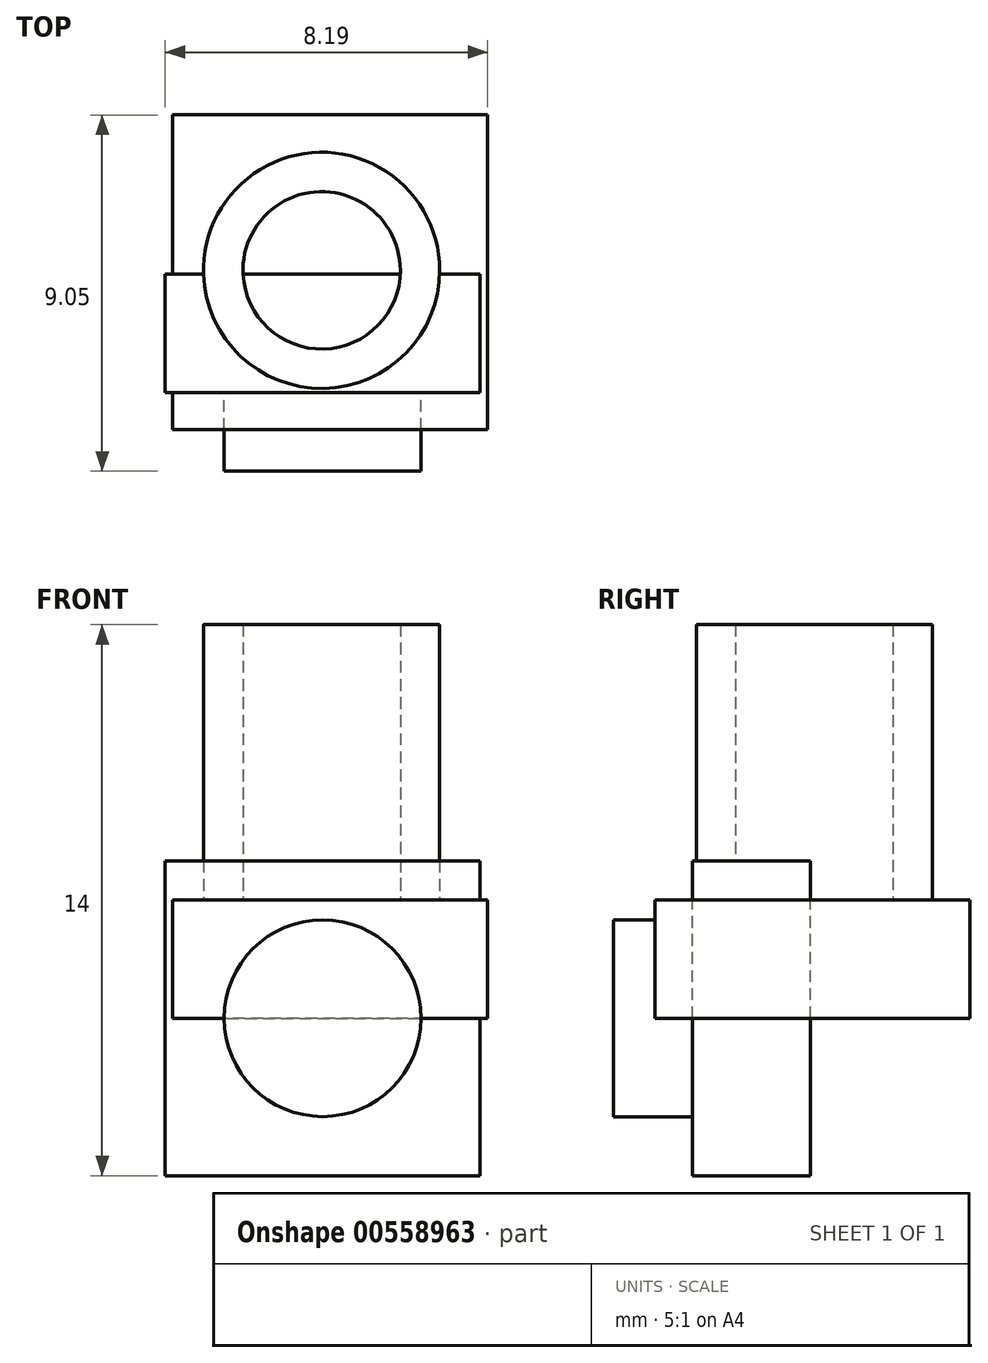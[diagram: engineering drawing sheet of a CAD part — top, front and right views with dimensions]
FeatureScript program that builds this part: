
annotation { "Feature Type Name" : "Feature", "Feature Type Description" : "" }
export const myFeature = defineFeature(function(context is Context, id is Id, definition is map)
    precondition{}
    {
        {
            var Q0;
            Q0=qCreatedBy(makeId("Front.planeOp"),FACE);
            var sketch = newSketch(context, id + "F0", { "sketchPlane" : qUnion([Q0])});
            skLineSegment(sketch, "E0.bottom", {"start": v(4, 4) * mm, "end": v(-4, 4) * mm});
            skLineSegment(sketch, "E0.top", {"start": v(4, -4) * mm, "end": v(-4, -4) * mm});
            skLineSegment(sketch, "E0.left", {"start": v(4, 4) * mm, "end": v(4, -4) * mm});
            skLineSegment(sketch, "E0.right", {"start": v(-4, 4) * mm, "end": v(-4, -4) * mm});
            skPoint(sketch, "E0.middle", {"position": v(0, 0) * mm});
            skSolve(sketch);
        }
        {
            var Q0;
            Q0 = qSketchRegion(id + "F0", true);
            extrude(context, id + "F1", {"entities" : qUnion([Q0]), "depth" : 3 * mm, "offsetDistance" : 25 * mm});
        }
        {
            var Q0;
            Q0=qCreatedBy(makeId("Front.planeOp"),FACE);
            var sketch = newSketch(context, id + "F2", { "sketchPlane" : qUnion([Q0])});
            skCircle(sketch, "E1", {"center": v(0, 0) * mm, "radius": 2.5 * mm});
            skSolve(sketch);
        }
        {
            var Q0;
            Q0 = qSketchRegion(id + "F2", true);
            extrude(context, id + "F3", {"entities" : qUnion([Q0]), "operationType" : NewBodyOperationType.ADD, "depth" : 5 * mm, "offsetDistance" : 25 * mm});
        }
        {
            var Q0;
            Q0=qCreatedBy(makeId("Top.planeOp"),FACE);
            var sketch = newSketch(context, id + "F4", { "sketchPlane" : qUnion([Q0])});
            skLineSegment(sketch, "E2.bottom", {"start": v(-3.81, 4.05) * mm, "end": v(4.19, 4.05) * mm});
            skLineSegment(sketch, "E2.top", {"start": v(-3.81, -3.95) * mm, "end": v(4.19, -3.95) * mm});
            skLineSegment(sketch, "E2.left", {"start": v(-3.81, 4.05) * mm, "end": v(-3.81, -3.95) * mm});
            skLineSegment(sketch, "E2.right", {"start": v(4.19, 4.05) * mm, "end": v(4.19, -3.95) * mm});
            skPoint(sketch, "E2.middle", {"position": v(0.19, 0.05) * mm});
            skSolve(sketch);
        }
        {
            var Q0;
            Q0 = qSketchRegion(id + "F4", true);
            extrude(context, id + "F5", {"entities" : qUnion([Q0]), "depth" : 3 * mm, "offsetDistance" : 25 * mm});
        }
        {
            var Q0;
            Q0=qCreatedBy(makeId("Top.planeOp"),FACE);
            var sketch = newSketch(context, id + "F6", { "sketchPlane" : qUnion([Q0])});
            skCircle(sketch, "E3", {"center": v(-0.03, 0.1) * mm, "radius": 3 * mm});
            skCircle(sketch, "E4", {"center": v(-0.03, 0.1) * mm, "radius": 2 * mm});
            skSolve(sketch);
        }
        {
            var Q0;
            Q0 = qSketchRegion(id + "F6", true);
            extrude(context, id + "F7", {"entities" : qUnion([Q0]), "operationType" : NewBodyOperationType.ADD, "depth" : 10 * mm, "offsetDistance" : 25 * mm});
        }
    });
